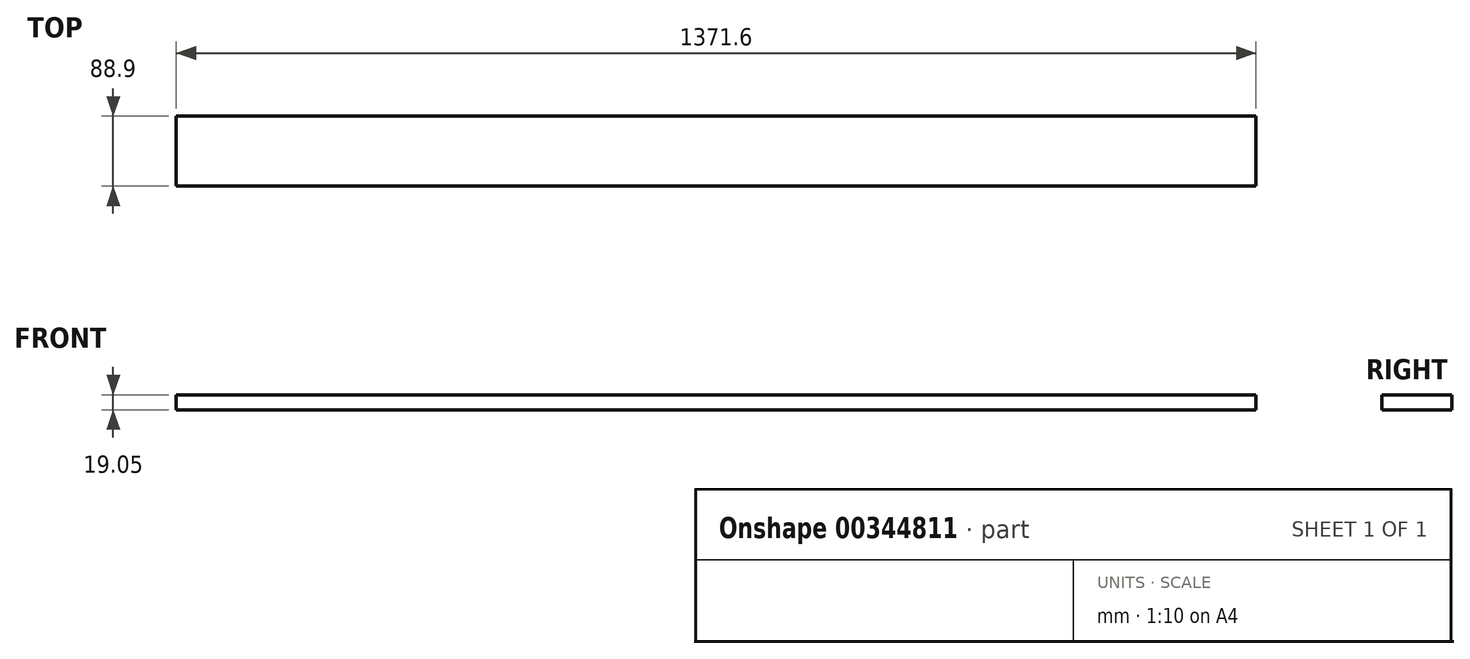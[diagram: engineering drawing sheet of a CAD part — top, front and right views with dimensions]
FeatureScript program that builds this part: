
annotation { "Feature Type Name" : "Feature", "Feature Type Description" : "" }
export const myFeature = defineFeature(function(context is Context, id is Id, definition is map)
    precondition{}
    {
        {
            var Q0;
            Q0=qCreatedBy(makeId("Right.planeOp"),FACE);
            var sketch = newSketch(context, id + "F0", { "sketchPlane" : qUnion([Q0])});
            skLineSegment(sketch, "E0.bottom", {"start": v(0, 0) * mm, "end": v(88.9, 0) * mm});
            skLineSegment(sketch, "E0.top", {"start": v(0, 19.05) * mm, "end": v(88.9, 19.05) * mm});
            skLineSegment(sketch, "E0.left", {"start": v(0, 0) * mm, "end": v(0, 19.05) * mm});
            skLineSegment(sketch, "E0.right", {"start": v(88.9, 0) * mm, "end": v(88.9, 19.05) * mm});
            skSolve(sketch);
        }
        {
            var Q0;
            Q0=makeQuery(id+"F0.imprint","IMPRINT",FACE,{"disambiguationData":[TD([[makeQuery(id+"F0.imprint","IMPRINT",EDGE,{"derivedFrom":sQuery(id+"F0.wireOp",EDGE,"E0.bottom")}),1.0]])]});
            extrude(context, id + "F1", {"entities" : qUnion([Q0]), "depth" : 1371.6 * mm});
        }
    });
